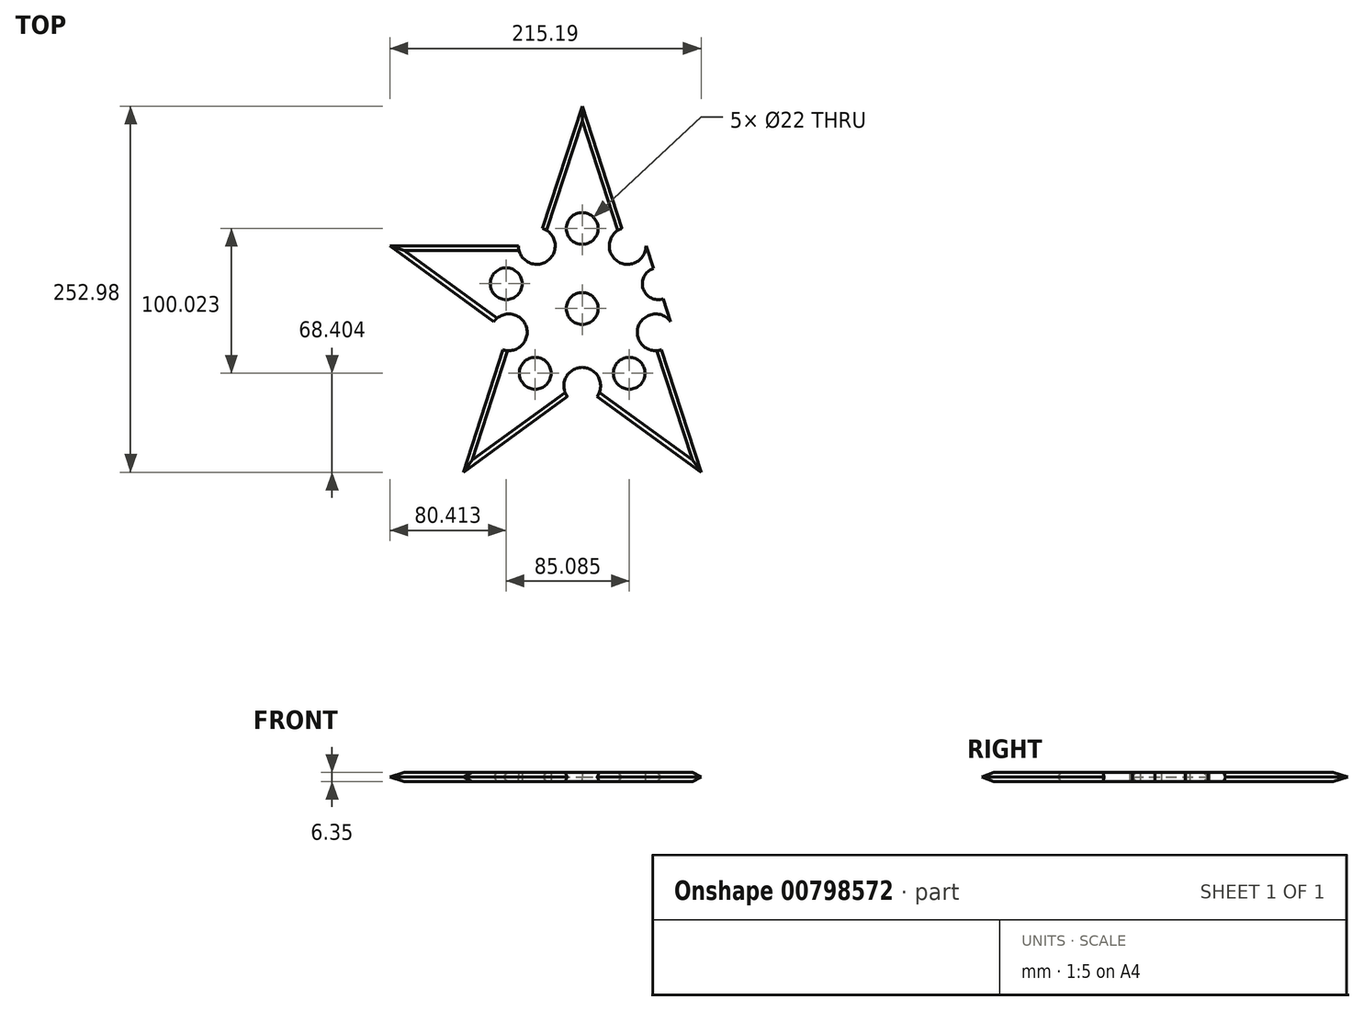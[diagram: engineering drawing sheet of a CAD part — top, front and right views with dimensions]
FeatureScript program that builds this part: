
annotation { "Feature Type Name" : "Feature", "Feature Type Description" : "" }
export const myFeature = defineFeature(function(context is Context, id is Id, definition is map)
    precondition{}
    {
        {
            var Q0;
            Q0=qCreatedBy(makeId("Top.planeOp"),FACE);
            var sketch = newSketch(context, id + "F0", { "sketchPlane" : qUnion([Q0])});
            skLineSegment(sketch, "E0", {"start": v(-12.03, 59.72) * mm, "end": v(19.37, 156.35) * mm});
            skLineSegment(sketch, "E1", {"start": v(19.37, 156.35) * mm, "end": v(50.76, 59.72) * mm});
            skLineSegment(sketch, "E2", {"start": v(50.76, 59.72) * mm, "end": v(152.36, 59.72) * mm});
            skLineSegment(sketch, "E3", {"start": v(152.36, 59.72) * mm, "end": v(70.17, 0) * mm});
            skLineSegment(sketch, "E4", {"start": v(70.17, 0) * mm, "end": v(101.56, -96.63) * mm});
            skLineSegment(sketch, "E5", {"start": v(101.56, -96.63) * mm, "end": v(19.37, -36.9) * mm});
            skLineSegment(sketch, "E6", {"start": v(19.37, -36.9) * mm, "end": v(-62.83, -96.63) * mm});
            skLineSegment(sketch, "E7", {"start": v(-62.83, -96.63) * mm, "end": v(-31.43, 0) * mm});
            skLineSegment(sketch, "E8", {"start": v(-31.43, 0) * mm, "end": v(-113.63, 59.72) * mm});
            skLineSegment(sketch, "E9", {"start": v(-113.63, 59.72) * mm, "end": v(-12.03, 59.72) * mm});
            skLineSegment(sketch, "E10", {"start": v(-12.03, 59.72) * mm, "end": v(50.76, 59.72) * mm});
            skCircle(sketch, "E11", {"center": v(-31.43, 0) * mm, "radius": 12.7 * mm});
            skCircle(sketch, "E12", {"center": v(-12.03, 59.72) * mm, "radius": 12.7 * mm});
            skCircle(sketch, "E13", {"center": v(50.76, 59.72) * mm, "radius": 12.7 * mm});
            skCircle(sketch, "E14", {"center": v(70.17, 0) * mm, "radius": 12.7 * mm});
            skCircle(sketch, "E15", {"center": v(19.37, -36.9) * mm, "radius": 12.7 * mm});
            skLineSegment(sketch, "E16", {"start": v(-31.43, 0) * mm, "end": v(152.36, 59.72) * mm});
            skLineSegment(sketch, "E17", {"start": v(101.56, -96.63) * mm, "end": v(-12.03, 59.72) * mm});
            skLineSegment(sketch, "E18", {"start": v(-62.83, -96.63) * mm, "end": v(50.76, 59.72) * mm});
            skLineSegment(sketch, "E19", {"start": v(-113.63, 59.72) * mm, "end": v(70.17, 0) * mm});
            skLineSegment(sketch, "E20", {"start": v(19.37, 156.35) * mm, "end": v(19.37, -36.9) * mm});
            skPoint(sketch, "E21", {"position": v(19.37, 16.5) * mm});
            skCircle(sketch, "E22", {"center": v(19.37, 16.5) * mm, "radius": 11 * mm});
            skPoint(sketch, "E23", {"position": v(-41.7, 7.46) * mm});
            skPoint(sketch, "E24", {"position": v(-24.73, 59.72) * mm});
            skPoint(sketch, "E25", {"position": v(-8.1, 71.8) * mm});
            skPoint(sketch, "E26", {"position": v(46.84, 71.8) * mm});
            skPoint(sketch, "E27", {"position": v(63.46, 59.72) * mm});
            skPoint(sketch, "E28", {"position": v(80.44, 7.46) * mm});
            skPoint(sketch, "E29", {"position": v(74.1, -12.08) * mm});
            skPoint(sketch, "E30", {"position": v(29.64, -44.37) * mm});
            skPoint(sketch, "E31", {"position": v(9.1, -44.37) * mm});
            skPoint(sketch, "E32", {"position": v(-35.36, -12.08) * mm});
            skLineSegment(sketch, "E33", {"start": v(-35.36, -12.08) * mm, "end": v(9.1, -44.37) * mm});
            skLineSegment(sketch, "E34", {"start": v(29.64, -44.37) * mm, "end": v(74.1, -12.08) * mm});
            skLineSegment(sketch, "E35", {"start": v(80.44, 7.46) * mm, "end": v(63.46, 59.72) * mm});
            skLineSegment(sketch, "E36", {"start": v(46.84, 71.8) * mm, "end": v(-8.1, 71.8) * mm});
            skLineSegment(sketch, "E37", {"start": v(-24.73, 59.72) * mm, "end": v(-41.7, 7.46) * mm});
            skCircle(sketch, "E38", {"center": v(71.95, 33.6) * mm, "radius": 11 * mm});
            skCircle(sketch, "E39", {"center": v(19.37, 71.8) * mm, "radius": 11 * mm});
            skCircle(sketch, "E40", {"center": v(-33.22, 33.6) * mm, "radius": 11 * mm});
            skCircle(sketch, "E41", {"center": v(-13.13, -28.23) * mm, "radius": 11 * mm});
            skCircle(sketch, "E42", {"center": v(51.87, -28.23) * mm, "radius": 11 * mm});
            skSolve(sketch);
        }
        {
            var Q0;
            {var subQ0=sQuery(id+"F0.wireOp",EDGE,"E1");var subQ1=sQuery(id+"F0.wireOp",EDGE,"E0");var subQ2=makeQuery(id+"F0.imprint","INTERSECT",VERTEX,{"derivedFrom":[subQ1,subQ0]});Q0=makeQuery(id+"F0.imprint","IMPRINT",FACE,{"disambiguationData":[TD([[makeQuery(id+"F0.imprint","IMPRINT",EDGE,{"disambiguationData":[TD([[subQ2,1.0]])],"derivedFrom":subQ1}),-1.0]])]});}
            var Q1;
            Q1=makeQuery(id+"F0.imprint","IMPRINT",FACE,{"disambiguationData":[TD([[makeQuery(id+"F0.imprint","IMPRINT",EDGE,{"derivedFrom":sQuery(id+"F0.wireOp",EDGE,"4qmwU5QX-Krty-CmfF-glWq-TSzqoq6GpiW4")}),-1.0]])]});
            var Q2;
            {var subQ0=sQuery(id+"F0.wireOp",EDGE,"E20");var subQ5=sQuery(id+"F0.wireOp",EDGE,"E10");var subQ6=makeQuery(id+"F0.imprint","INTERSECT",VERTEX,{"derivedFrom":[subQ5,subQ0]});Q2=makeQuery(id+"F0.imprint","IMPRINT",FACE,{"disambiguationData":[TD([[makeQuery(id+"F0.imprint","IMPRINT",EDGE,{"disambiguationData":[TD([[subQ6,-1.0]])],"derivedFrom":subQ5}),1.0]])]});}
            var Q3;
            {var subQ1=sQuery(id+"F0.wireOp",EDGE,"E10");var subQ6=sQuery(id+"F0.wireOp",EDGE,"E12");var subQ9=makeQuery(id+"F0.imprint","INTERSECT",VERTEX,{"derivedFrom":[subQ1,subQ6]});Q3=makeQuery(id+"F0.imprint","IMPRINT",FACE,{"disambiguationData":[TD([[makeQuery(id+"F0.imprint","IMPRINT",EDGE,{"disambiguationData":[TD([[subQ9,-1.0]])],"derivedFrom":subQ1}),-1.0]])]});}
            var Q4;
            {var subQ1=sQuery(id+"F0.wireOp",EDGE,"E9");var subQ6=sQuery(id+"F0.wireOp",EDGE,"E12");var subQ9=makeQuery(id+"F0.imprint","INTERSECT",VERTEX,{"derivedFrom":[subQ1,subQ6]});Q4=makeQuery(id+"F0.imprint","IMPRINT",FACE,{"disambiguationData":[TD([[makeQuery(id+"F0.imprint","IMPRINT",EDGE,{"disambiguationData":[TD([[subQ9,-1.0]])],"derivedFrom":subQ6}),-1.0]])]});}
            var Q5;
            {var subQ1=sQuery(id+"F0.wireOp",EDGE,"E8");var subQ5=sQuery(id+"F0.wireOp",EDGE,"E11");var subQ6=makeQuery(id+"F0.imprint","INTERSECT",VERTEX,{"derivedFrom":[subQ1,subQ5]});Q5=makeQuery(id+"F0.imprint","IMPRINT",FACE,{"disambiguationData":[TD([[makeQuery(id+"F0.imprint","IMPRINT",EDGE,{"disambiguationData":[TD([[subQ6,1.0]])],"derivedFrom":subQ5}),-1.0]])]});}
            var Q6;
            {var subQ1=sQuery(id+"F0.wireOp",EDGE,"E11");var subQ6=sQuery(id+"F0.wireOp",EDGE,"E7");var subQ9=makeQuery(id+"F0.imprint","INTERSECT",VERTEX,{"derivedFrom":[subQ6,subQ1]});Q6=makeQuery(id+"F0.imprint","IMPRINT",FACE,{"disambiguationData":[TD([[makeQuery(id+"F0.imprint","IMPRINT",EDGE,{"disambiguationData":[TD([[subQ9,-1.0]])],"derivedFrom":subQ1}),-1.0]])]});}
            var Q7;
            {var subQ1=sQuery(id+"F0.wireOp",EDGE,"E15");var subQ6=sQuery(id+"F0.wireOp",EDGE,"E6");var subQ9=makeQuery(id+"F0.imprint","INTERSECT",VERTEX,{"derivedFrom":[subQ6,subQ1]});Q7=makeQuery(id+"F0.imprint","IMPRINT",FACE,{"disambiguationData":[TD([[makeQuery(id+"F0.imprint","IMPRINT",EDGE,{"disambiguationData":[TD([[subQ9,1.0]])],"derivedFrom":subQ1}),-1.0]])]});}
            var Q8;
            {var subQ1=sQuery(id+"F0.wireOp",EDGE,"E5");var subQ6=sQuery(id+"F0.wireOp",EDGE,"E15");var subQ9=makeQuery(id+"F0.imprint","INTERSECT",VERTEX,{"derivedFrom":[subQ1,subQ6]});Q8=makeQuery(id+"F0.imprint","IMPRINT",FACE,{"disambiguationData":[TD([[makeQuery(id+"F0.imprint","IMPRINT",EDGE,{"disambiguationData":[TD([[subQ9,-1.0]])],"derivedFrom":subQ6}),-1.0]])]});}
            var Q9;
            {var subQ1=sQuery(id+"F0.wireOp",EDGE,"E4");var subQ5=sQuery(id+"F0.wireOp",EDGE,"E14");var subQ6=makeQuery(id+"F0.imprint","INTERSECT",VERTEX,{"derivedFrom":[subQ1,subQ5]});Q9=makeQuery(id+"F0.imprint","IMPRINT",FACE,{"disambiguationData":[TD([[makeQuery(id+"F0.imprint","IMPRINT",EDGE,{"disambiguationData":[TD([[subQ6,1.0]])],"derivedFrom":subQ5}),-1.0]])]});}
            var Q10;
            {var subQ1=sQuery(id+"F0.wireOp",EDGE,"E14");var subQ6=sQuery(id+"F0.wireOp",EDGE,"E3");var subQ9=makeQuery(id+"F0.imprint","INTERSECT",VERTEX,{"derivedFrom":[subQ6,subQ1]});Q10=makeQuery(id+"F0.imprint","IMPRINT",FACE,{"disambiguationData":[TD([[makeQuery(id+"F0.imprint","IMPRINT",EDGE,{"disambiguationData":[TD([[subQ9,-1.0]])],"derivedFrom":subQ1}),-1.0]])]});}
            var Q11;
            {var subQ1=sQuery(id+"F0.wireOp",EDGE,"E13");var subQ5=sQuery(id+"F0.wireOp",EDGE,"E2");var subQ6=makeQuery(id+"F0.imprint","INTERSECT",VERTEX,{"derivedFrom":[subQ5,subQ1]});Q11=makeQuery(id+"F0.imprint","IMPRINT",FACE,{"disambiguationData":[TD([[makeQuery(id+"F0.imprint","IMPRINT",EDGE,{"disambiguationData":[TD([[subQ6,1.0]])],"derivedFrom":subQ1}),-1.0]])]});}
            var Q12;
            {var subQ1=sQuery(id+"F0.wireOp",EDGE,"E12");var subQ7=sQuery(id+"F0.wireOp",EDGE,"E10");var subQ8=makeQuery(id+"F0.imprint","INTERSECT",VERTEX,{"derivedFrom":[subQ7,subQ1]});Q12=makeQuery(id+"F0.imprint","IMPRINT",FACE,{"disambiguationData":[TD([[makeQuery(id+"F0.imprint","IMPRINT",EDGE,{"disambiguationData":[TD([[subQ8,-1.0]])],"derivedFrom":subQ7}),1.0]])]});}
            var Q13;
            {var subQ0=sQuery(id+"F0.wireOp",EDGE,"E20");var subQ5=sQuery(id+"F0.wireOp",EDGE,"E39");var subQ6=makeQuery(id+"F0.imprint","INTERSECT",VERTEX,{"disambiguationData":[OD(0.0)],"derivedFrom":[subQ0,subQ5]});Q13=makeQuery(id+"F0.imprint","IMPRINT",FACE,{"disambiguationData":[TD([[makeQuery(id+"F0.imprint","IMPRINT",EDGE,{"disambiguationData":[TD([[subQ6,1.0]])],"derivedFrom":subQ5}),-1.0]])]});}
            var Q14;
            {var subQ5=sQuery(id+"F0.wireOp",EDGE,"E10");var subQ7=sQuery(id+"F0.wireOp",EDGE,"E20");var subQ8=makeQuery(id+"F0.imprint","INTERSECT",VERTEX,{"derivedFrom":[subQ5,subQ7]});Q14=makeQuery(id+"F0.imprint","IMPRINT",FACE,{"disambiguationData":[TD([[makeQuery(id+"F0.imprint","IMPRINT",EDGE,{"disambiguationData":[TD([[subQ8,-1.0]])],"derivedFrom":subQ5}),-1.0]])]});}
            var Q15;
            {var subQ0=sQuery(id+"F0.wireOp",EDGE,"E19");var subQ5=sQuery(id+"F0.wireOp",EDGE,"E40");var subQ7=makeQuery(id+"F0.imprint","INTERSECT",VERTEX,{"disambiguationData":[OD(0.0)],"derivedFrom":[subQ0,subQ5]});Q15=makeQuery(id+"F0.imprint","IMPRINT",FACE,{"disambiguationData":[TD([[makeQuery(id+"F0.imprint","IMPRINT",EDGE,{"disambiguationData":[TD([[subQ7,1.0]])],"derivedFrom":subQ5}),-1.0]])]});}
            var Q16;
            {var subQ0=sQuery(id+"F0.wireOp",EDGE,"E19");var subQ5=sQuery(id+"F0.wireOp",EDGE,"E40");var subQ6=makeQuery(id+"F0.imprint","INTERSECT",VERTEX,{"disambiguationData":[OD(0.0)],"derivedFrom":[subQ0,subQ5]});Q16=makeQuery(id+"F0.imprint","IMPRINT",FACE,{"disambiguationData":[TD([[makeQuery(id+"F0.imprint","IMPRINT",EDGE,{"disambiguationData":[TD([[subQ6,-1.0]])],"derivedFrom":subQ5}),-1.0]])]});}
            var Q17;
            {var subQ0=sQuery(id+"F0.wireOp",EDGE,"E18");var subQ5=sQuery(id+"F0.wireOp",EDGE,"E41");var subQ6=makeQuery(id+"F0.imprint","INTERSECT",VERTEX,{"disambiguationData":[OD(0.0)],"derivedFrom":[subQ0,subQ5]});Q17=makeQuery(id+"F0.imprint","IMPRINT",FACE,{"disambiguationData":[TD([[makeQuery(id+"F0.imprint","IMPRINT",EDGE,{"disambiguationData":[TD([[subQ6,1.0]])],"derivedFrom":subQ5}),-1.0]])]});}
            var Q18;
            {var subQ0=sQuery(id+"F0.wireOp",EDGE,"E18");var subQ5=sQuery(id+"F0.wireOp",EDGE,"E41");var subQ6=makeQuery(id+"F0.imprint","INTERSECT",VERTEX,{"disambiguationData":[OD(0.0)],"derivedFrom":[subQ0,subQ5]});Q18=makeQuery(id+"F0.imprint","IMPRINT",FACE,{"disambiguationData":[TD([[makeQuery(id+"F0.imprint","IMPRINT",EDGE,{"disambiguationData":[TD([[subQ6,-1.0]])],"derivedFrom":subQ5}),-1.0]])]});}
            var Q19;
            {var subQ0=sQuery(id+"F0.wireOp",EDGE,"E17");var subQ5=sQuery(id+"F0.wireOp",EDGE,"E42");var subQ6=makeQuery(id+"F0.imprint","INTERSECT",VERTEX,{"disambiguationData":[OD(0.0)],"derivedFrom":[subQ0,subQ5]});Q19=makeQuery(id+"F0.imprint","IMPRINT",FACE,{"disambiguationData":[TD([[makeQuery(id+"F0.imprint","IMPRINT",EDGE,{"disambiguationData":[TD([[subQ6,1.0]])],"derivedFrom":subQ5}),-1.0]])]});}
            var Q20;
            {var subQ0=sQuery(id+"F0.wireOp",EDGE,"E17");var subQ5=sQuery(id+"F0.wireOp",EDGE,"E42");var subQ6=makeQuery(id+"F0.imprint","INTERSECT",VERTEX,{"disambiguationData":[OD(0.0)],"derivedFrom":[subQ0,subQ5]});Q20=makeQuery(id+"F0.imprint","IMPRINT",FACE,{"disambiguationData":[TD([[makeQuery(id+"F0.imprint","IMPRINT",EDGE,{"disambiguationData":[TD([[subQ6,-1.0]])],"derivedFrom":subQ5}),-1.0]])]});}
            var Q21;
            {var subQ0=sQuery(id+"F0.wireOp",EDGE,"E16");var subQ5=sQuery(id+"F0.wireOp",EDGE,"E38");var subQ6=makeQuery(id+"F0.imprint","INTERSECT",VERTEX,{"disambiguationData":[OD(1.0)],"derivedFrom":[subQ0,subQ5]});Q21=makeQuery(id+"F0.imprint","IMPRINT",FACE,{"disambiguationData":[TD([[makeQuery(id+"F0.imprint","IMPRINT",EDGE,{"disambiguationData":[TD([[subQ6,1.0]])],"derivedFrom":subQ5}),-1.0]])]});}
            var Q22;
            {var subQ0=sQuery(id+"F0.wireOp",EDGE,"E16");var subQ5=sQuery(id+"F0.wireOp",EDGE,"E38");var subQ6=makeQuery(id+"F0.imprint","INTERSECT",VERTEX,{"disambiguationData":[OD(1.0)],"derivedFrom":[subQ0,subQ5]});Q22=makeQuery(id+"F0.imprint","IMPRINT",FACE,{"disambiguationData":[TD([[makeQuery(id+"F0.imprint","IMPRINT",EDGE,{"disambiguationData":[TD([[subQ6,-1.0]])],"derivedFrom":subQ5}),-1.0]])]});}
            extrude(context, id + "F1", {"entities" : qUnion([Q0, Q1, Q2, Q3, Q4, Q5, Q6, Q7, Q8, Q9, Q10, Q11, Q12, Q13, Q14, Q15, Q16, Q17, Q18, Q19, Q20, Q21, Q22]), "depth" : 6.35 * mm, "offsetDistance" : 30.48 * mm});
        }
        {
            var Q0;
            Q0=makeQuery(id+"F1.opExtrude","CAP_EDGE",EDGE,{"disambiguationData":[OSD([sQuery(id+"F0.wireOp",EDGE,"E8")])],"isStart":false});
            var Q1;
            Q1=makeQuery(id+"F1.opExtrude","CAP_EDGE",EDGE,{"disambiguationData":[OSD([sQuery(id+"F0.wireOp",EDGE,"E9")])],"isStart":false});
            var Q2;
            Q2=makeQuery(id+"F1.opExtrude","CAP_EDGE",EDGE,{"disambiguationData":[OSD([sQuery(id+"F0.wireOp",EDGE,"E0")])],"isStart":false});
            var Q3;
            Q3=makeQuery(id+"F1.opExtrude","CAP_EDGE",EDGE,{"disambiguationData":[OSD([sQuery(id+"F0.wireOp",EDGE,"E1")])],"isStart":false});
            var Q4;
            Q4=makeQuery(id+"F1.opExtrude","CAP_EDGE",EDGE,{"disambiguationData":[OSD([sQuery(id+"F0.wireOp",EDGE,"E2")])],"isStart":false});
            var Q5;
            Q5=makeQuery(id+"F1.opExtrude","CAP_EDGE",EDGE,{"disambiguationData":[OSD([sQuery(id+"F0.wireOp",EDGE,"E3")])],"isStart":false});
            var Q6;
            Q6=makeQuery(id+"F1.opExtrude","CAP_EDGE",EDGE,{"disambiguationData":[OSD([sQuery(id+"F0.wireOp",EDGE,"E4")])],"isStart":false});
            var Q7;
            Q7=makeQuery(id+"F1.opExtrude","CAP_EDGE",EDGE,{"disambiguationData":[OSD([sQuery(id+"F0.wireOp",EDGE,"E5")])],"isStart":false});
            var Q8;
            Q8=makeQuery(id+"F1.opExtrude","CAP_EDGE",EDGE,{"disambiguationData":[OSD([sQuery(id+"F0.wireOp",EDGE,"E6")])],"isStart":false});
            var Q9;
            Q9=makeQuery(id+"F1.opExtrude","CAP_EDGE",EDGE,{"disambiguationData":[OSD([sQuery(id+"F0.wireOp",EDGE,"E7")])],"isStart":false});
            var Q10;
            Q10=makeQuery(id+"F1.opExtrude","CAP_EDGE",EDGE,{"disambiguationData":[OSD([sQuery(id+"F0.wireOp",EDGE,"E6")])],"isStart":true});
            var Q11;
            Q11=makeQuery(id+"F1.opExtrude","CAP_EDGE",EDGE,{"disambiguationData":[OSD([sQuery(id+"F0.wireOp",EDGE,"E7")])],"isStart":true});
            var Q12;
            Q12=makeQuery(id+"F1.opExtrude","CAP_EDGE",EDGE,{"disambiguationData":[OSD([sQuery(id+"F0.wireOp",EDGE,"E5")])],"isStart":true});
            var Q13;
            Q13=makeQuery(id+"F1.opExtrude","CAP_EDGE",EDGE,{"disambiguationData":[OSD([sQuery(id+"F0.wireOp",EDGE,"E4")])],"isStart":true});
            var Q14;
            Q14=makeQuery(id+"F1.opExtrude","CAP_EDGE",EDGE,{"disambiguationData":[OSD([sQuery(id+"F0.wireOp",EDGE,"E3")])],"isStart":true});
            var Q15;
            Q15=makeQuery(id+"F1.opExtrude","CAP_EDGE",EDGE,{"disambiguationData":[OSD([sQuery(id+"F0.wireOp",EDGE,"E2")])],"isStart":true});
            var Q16;
            Q16=makeQuery(id+"F1.opExtrude","CAP_EDGE",EDGE,{"disambiguationData":[OSD([sQuery(id+"F0.wireOp",EDGE,"E1")])],"isStart":true});
            var Q17;
            Q17=makeQuery(id+"F1.opExtrude","CAP_EDGE",EDGE,{"disambiguationData":[OSD([sQuery(id+"F0.wireOp",EDGE,"E0")])],"isStart":true});
            var Q18;
            Q18=makeQuery(id+"F1.opExtrude","CAP_EDGE",EDGE,{"disambiguationData":[OSD([sQuery(id+"F0.wireOp",EDGE,"E9")])],"isStart":true});
            var Q19;
            Q19=makeQuery(id+"F1.opExtrude","CAP_EDGE",EDGE,{"disambiguationData":[OSD([sQuery(id+"F0.wireOp",EDGE,"E8")])],"isStart":true});
            chamfer(context, id + "F2", {"entities" : qUnion([Q0, Q1, Q2, Q3, Q4, Q5, Q6, Q7, Q8, Q9, Q10, Q11, Q12, Q13, Q14, Q15, Q16, Q17, Q18, Q19]), "width" : 3.17 * mm, "tangentPropagation" : true});
        }
    });
